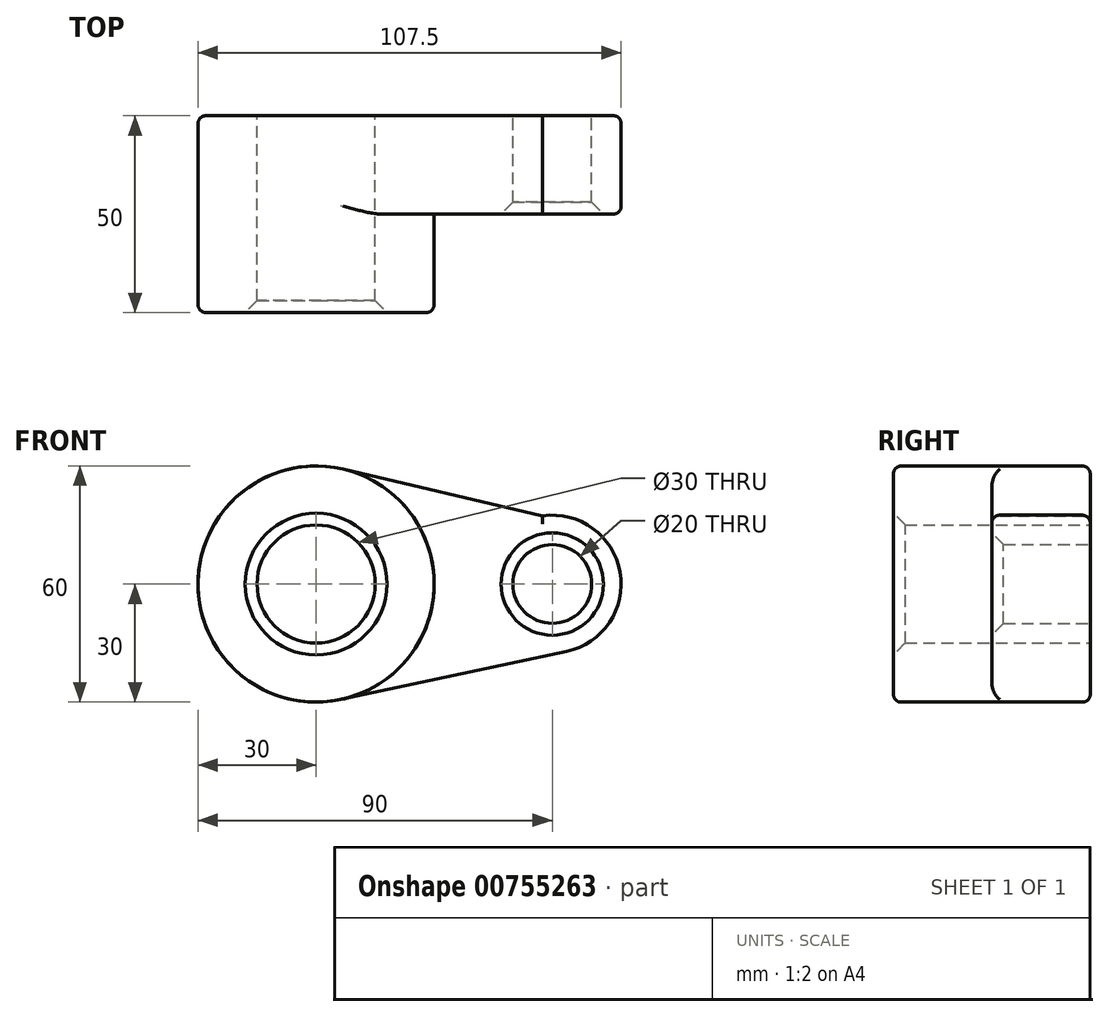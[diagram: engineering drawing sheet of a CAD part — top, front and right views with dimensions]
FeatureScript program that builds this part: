
annotation { "Feature Type Name" : "Feature", "Feature Type Description" : "" }
export const myFeature = defineFeature(function(context is Context, id is Id, definition is map)
    precondition{}
    {
        {
            var Q0;
            Q0=qCreatedBy(makeId("Front.planeOp"),FACE);
            var sketch = newSketch(context, id + "F0", { "sketchPlane" : qUnion([Q0])});
            skCircle(sketch, "E0", {"center": v(0, 0) * mm, "radius": 30 * mm});
            skCircle(sketch, "E1", {"center": v(60, 0) * mm, "radius": 17.5 * mm});
            skLineSegment(sketch, "E2", {"start": v(6.85, 29.2) * mm, "end": v(57.54, 17.33) * mm});
            skLineSegment(sketch, "E3", {"start": v(6.25, -29.34) * mm, "end": v(63.65, -17.12) * mm});
            skCircle(sketch, "E4", {"center": v(0, 0) * mm, "radius": 15 * mm});
            skCircle(sketch, "E5", {"center": v(60, 0) * mm, "radius": 10 * mm});
            skSolve(sketch);
        }
        {
            var Q0;
            Q0=makeQuery(id+"F0.imprint","IMPRINT",FACE,{"disambiguationData":[TD([[makeQuery(id+"F0.imprint","IMPRINT",EDGE,{"derivedFrom":sQuery(id+"F0.wireOp",EDGE,"E4")}),-1.0]])]});
            extrude(context, id + "F1", {"entities" : qUnion([Q0]), "depth" : 50 * mm, "offsetDistance" : 25 * mm});
        }
        {
            var Q0;
            Q0 = qSketchRegion(id + "F0", true);
            extrude(context, id + "F2", {"entities" : qUnion([Q0]), "operationType" : NewBodyOperationType.ADD, "depth" : 25 * mm, "offsetDistance" : 25 * mm});
        }
        {
            var Q0;
            Q0=makeQuery(id+"F2.opExtrude","CAP_EDGE",EDGE,{"disambiguationData":[OSD([sQuery(id+"F0.wireOp",EDGE,"E3")])],"isStart":false});
            var Q1;
            Q1=makeQuery(id+"F2.opExtrude","CAP_EDGE",EDGE,{"disambiguationData":[OSD([sQuery(id+"F0.wireOp",EDGE,"E3")])],"isStart":true});
            var Q2;
            Q2=makeQuery(id+"F1.opExtrude","CAP_EDGE",EDGE,{"disambiguationData":[OSD([sQuery(id+"F0.wireOp",EDGE,"E0")])],"isStart":true});
            var Q3;
            Q3=makeQuery(id+"F2.opExtrude","CAP_EDGE",EDGE,{"disambiguationData":[OSD([sQuery(id+"F0.wireOp",EDGE,"E1")])],"isStart":true});
            var Q4;
            Q4=makeQuery(id+"F2.opExtrude","CAP_EDGE",EDGE,{"disambiguationData":[OSD([sQuery(id+"F0.wireOp",EDGE,"E2")])],"isStart":false});
            var Q5;
            Q5=makeQuery(id+"F2.opExtrude","CAP_EDGE",EDGE,{"disambiguationData":[OSD([sQuery(id+"F0.wireOp",EDGE,"E1")])],"isStart":false});
            var Q6;
            Q6=makeQuery(id+"F2.opExtrude","CAP_EDGE",EDGE,{"disambiguationData":[OSD([sQuery(id+"F0.wireOp",EDGE,"E2")])],"isStart":true});
            var Q7;
            Q7=makeQuery(id+"F1.opExtrude","CAP_EDGE",EDGE,{"disambiguationData":[OSD([sQuery(id+"F0.wireOp",EDGE,"E0")])],"isStart":false});
            fillet(context, id + "F3", {"entities" : qUnion([Q0, Q1, Q2, Q3, Q4, Q5, Q6, Q7]), "radius" : 2 * mm, "tangentPropagation" : true, "allowEdgeOverflow" : false});
        }
        {
            var Q0;
            Q0=makeQuery(id+"F2.opExtrude","CAP_EDGE",EDGE,{"disambiguationData":[OSD([sQuery(id+"F0.wireOp",EDGE,"E5")])],"isStart":false});
            var Q1;
            Q1=makeQuery(id+"F1.opExtrude","CAP_EDGE",EDGE,{"disambiguationData":[OSD([sQuery(id+"F0.wireOp",EDGE,"E4")])],"isStart":false});
            chamfer(context, id + "F4", {"entities" : qUnion([Q0, Q1]), "width" : 3 * mm, "tangentPropagation" : true});
        }
    });
